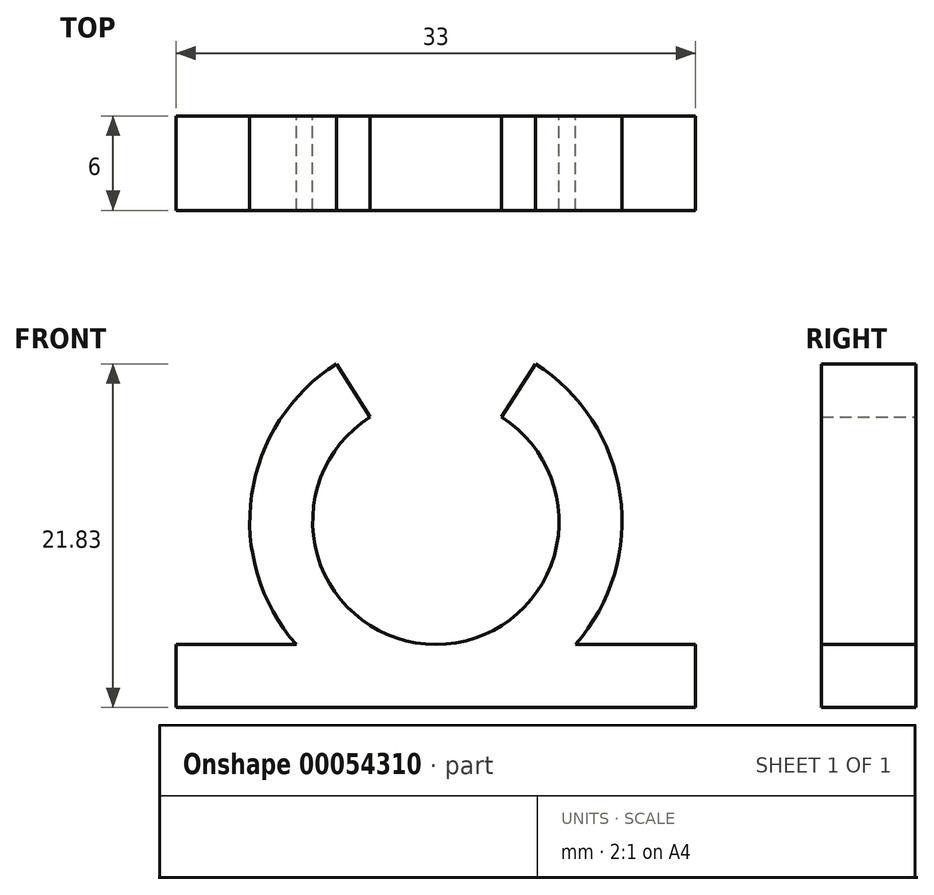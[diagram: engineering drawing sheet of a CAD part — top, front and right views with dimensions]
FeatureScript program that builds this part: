
annotation { "Feature Type Name" : "Feature", "Feature Type Description" : "" }
export const myFeature = defineFeature(function(context is Context, id is Id, definition is map)
    precondition{}
    {
        {
            var Q0;
            Q0=qCreatedBy(makeId("Front.planeOp"),FACE);
            var sketch = newSketch(context, id + "F0", { "sketchPlane" : qUnion([Q0])});
            skArc(sketch, "E0", {"start": v(-4.18, 6.62) * mm, "mid": v(-7.52, -2.17) * mm, "end": v(0, -7.83) * mm});
            skArc(sketch, "E1", {"start": v(-6.31, 10) * mm, "mid": v(-11.7, 1.68) * mm, "end": v(-8.87, -7.82) * mm});
            skPoint(sketch, "E2", {"position": v(-7.83, 0) * mm});
            skPoint(sketch, "E3", {"position": v(-11.82, 0) * mm});
            skLineSegment(sketch, "E4", {"start": v(0, -16.36) * mm, "end": v(0, 19.85) * mm, "construction": true});
            skPoint(sketch, "E5", {"position": v(-6.31, 10) * mm});
            skLineSegment(sketch, "E6", {"start": v(0, 0) * mm, "end": v(-6.31, 10) * mm, "construction": true});
            skPoint(sketch, "E7", {"position": v(-4.18, 6.62) * mm});
            skLineSegment(sketch, "E8", {"start": v(-4.18, 6.62) * mm, "end": v(-6.31, 10) * mm});
            skPoint(sketch, "E9", {"position": v(0, 11.82) * mm});
            skPoint(sketch, "E10", {"position": v(0, 7.83) * mm});
            skPoint(sketch, "E11", {"position": v(0, -7.83) * mm});
            skPoint(sketch, "E12", {"position": v(0, -11.82) * mm});
            skArc(sketch, "E13.MirrorCS", {"start": v(4.18, 6.62) * mm, "mid": v(7.52, -2.17) * mm, "end": v(0, -7.83) * mm});
            skLineSegment(sketch, "E14.MirrorCS", {"start": v(4.18, 6.62) * mm, "end": v(6.31, 10) * mm});
            skLineSegment(sketch, "E15.bottom", {"start": v(0, -11.82) * mm, "end": v(-16.5, -11.83) * mm});
            skLineSegment(sketch, "E15.top", {"start": v(-8.87, -7.83) * mm, "end": v(-16.5, -7.83) * mm});
            skLineSegment(sketch, "E15.right", {"start": v(-16.5, -11.83) * mm, "end": v(-16.5, -7.83) * mm});
            skPoint(sketch, "E16", {"position": v(-8.87, -7.83) * mm});
            skPoint(sketch, "E17.MirrorCS.start.orphan", {"position": v(6.31, 10) * mm});
            skLineSegment(sketch, "E18.MirrorCS", {"start": v(0, -11.82) * mm, "end": v(16.5, -11.83) * mm});
            skLineSegment(sketch, "E19.MirrorCS", {"start": v(16.5, -11.83) * mm, "end": v(16.5, -7.83) * mm});
            skLineSegment(sketch, "E20.MirrorCS", {"start": v(8.87, -7.83) * mm, "end": v(16.5, -7.83) * mm});
            skArc(sketch, "E21.MirrorCS", {"start": v(6.31, 10) * mm, "mid": v(11.7, 1.68) * mm, "end": v(8.87, -7.82) * mm});
            skSolve(sketch);
        }
        {
            var Q0;
            Q0 = qSketchRegion(id + "F0", true);
            extrude(context, id + "F1", {"entities" : qUnion([Q0]), "depth" : 6 * mm});
        }
    });
